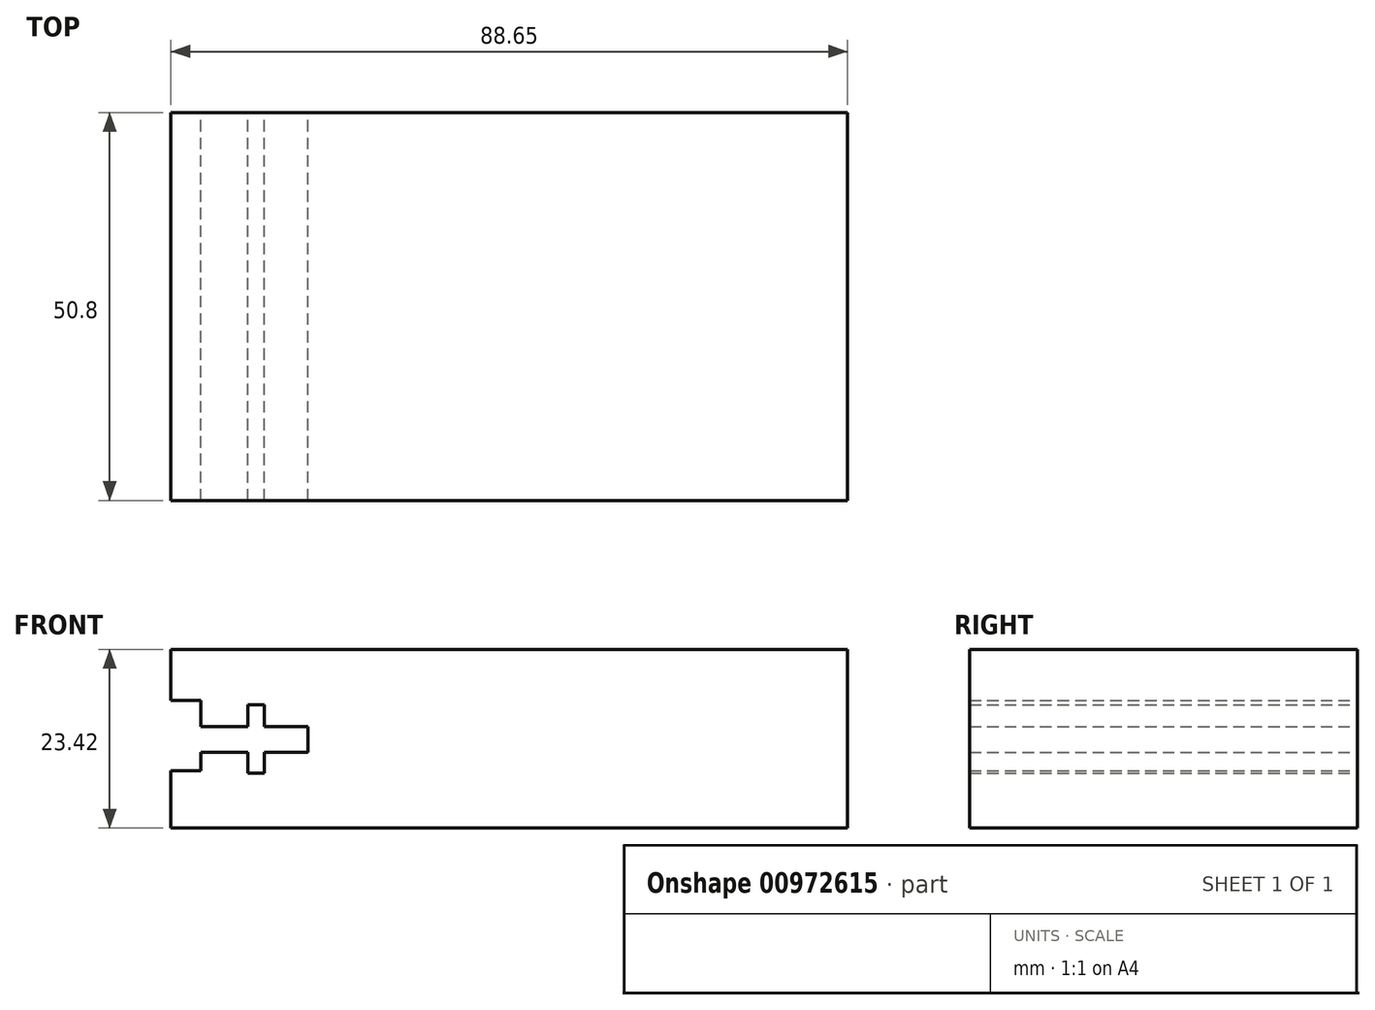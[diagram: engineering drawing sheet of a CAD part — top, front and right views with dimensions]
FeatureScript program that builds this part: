
annotation { "Feature Type Name" : "Feature", "Feature Type Description" : "" }
export const myFeature = defineFeature(function(context is Context, id is Id, definition is map)
    precondition{}
    {
        {
            var Q0;
            Q0=qCreatedBy(makeId("Front.planeOp"),FACE);
            var sketch = newSketch(context, id + "F0", { "sketchPlane" : qUnion([Q0])});
            skLineSegment(sketch, "E0.bottom", {"start": v(-17.98, 51.99) * mm, "end": v(70.67, 51.99) * mm});
            skLineSegment(sketch, "E0.top", {"start": v(-17.98, 28.57) * mm, "end": v(70.67, 28.57) * mm});
            skLineSegment(sketch, "E0.left", {"start": v(-17.98, 51.99) * mm, "end": v(-17.98, 45.3) * mm});
            skLineSegment(sketch, "E0.right", {"start": v(70.67, 51.99) * mm, "end": v(70.67, 28.57) * mm});
            skLineSegment(sketch, "E1.bottom", {"start": v(-17.98, 45.3) * mm, "end": v(-14.08, 45.3) * mm});
            skLineSegment(sketch, "E1.top", {"start": v(-17.98, 36.1) * mm, "end": v(-14.08, 36.1) * mm});
            skLineSegment(sketch, "E1.right", {"start": v(-14.08, 45.3) * mm, "end": v(-14.08, 36.1) * mm});
            skLineSegment(sketch, "E2.trimOffspring", {"start": v(-17.98, 36.1) * mm, "end": v(-17.98, 28.57) * mm});
            skLineSegment(sketch, "E3", {"start": v(-14.08, 41.89) * mm, "end": v(-7.89, 41.89) * mm});
            skLineSegment(sketch, "E4", {"start": v(-14.08, 38.54) * mm, "end": v(-7.89, 38.54) * mm});
            skLineSegment(sketch, "E5.bottom", {"start": v(-7.89, 44.75) * mm, "end": v(-5.72, 44.75) * mm});
            skLineSegment(sketch, "E5.top", {"start": v(-7.89, 35.78) * mm, "end": v(-5.72, 35.78) * mm});
            skLineSegment(sketch, "E5.left", {"start": v(-7.89, 44.75) * mm, "end": v(-7.89, 41.89) * mm});
            skLineSegment(sketch, "E5.right", {"start": v(-5.72, 44.75) * mm, "end": v(-5.72, 41.89) * mm});
            skLineSegment(sketch, "E6.trimOffspring", {"start": v(-5.72, 41.89) * mm, "end": v(0, 41.89) * mm});
            skLineSegment(sketch, "E7.trimOffspring", {"start": v(-5.72, 38.54) * mm, "end": v(0, 38.54) * mm});
            skLineSegment(sketch, "E8", {"start": v(0, 41.89) * mm, "end": v(0, 38.54) * mm});
            skLineSegment(sketch, "E9.trimOffspring", {"start": v(-7.89, 38.54) * mm, "end": v(-7.89, 35.78) * mm});
            skLineSegment(sketch, "E10.trimOffspring", {"start": v(-5.72, 38.54) * mm, "end": v(-5.72, 35.78) * mm});
            skSolve(sketch);
        }
        {
            var Q0;
            Q0=makeQuery(id+"F0.imprint","IMPRINT",FACE,{"disambiguationData":[TD([[makeQuery(id+"F0.imprint","IMPRINT",EDGE,{"derivedFrom":sQuery(id+"F0.wireOp",EDGE,"E0.bottom")}),-1.0]])]});
            extrude(context, id + "F1", {"entities" : qUnion([Q0]), "depth" : 50.8 * mm, "offsetDistance" : 25.4 * mm});
        }
    });
